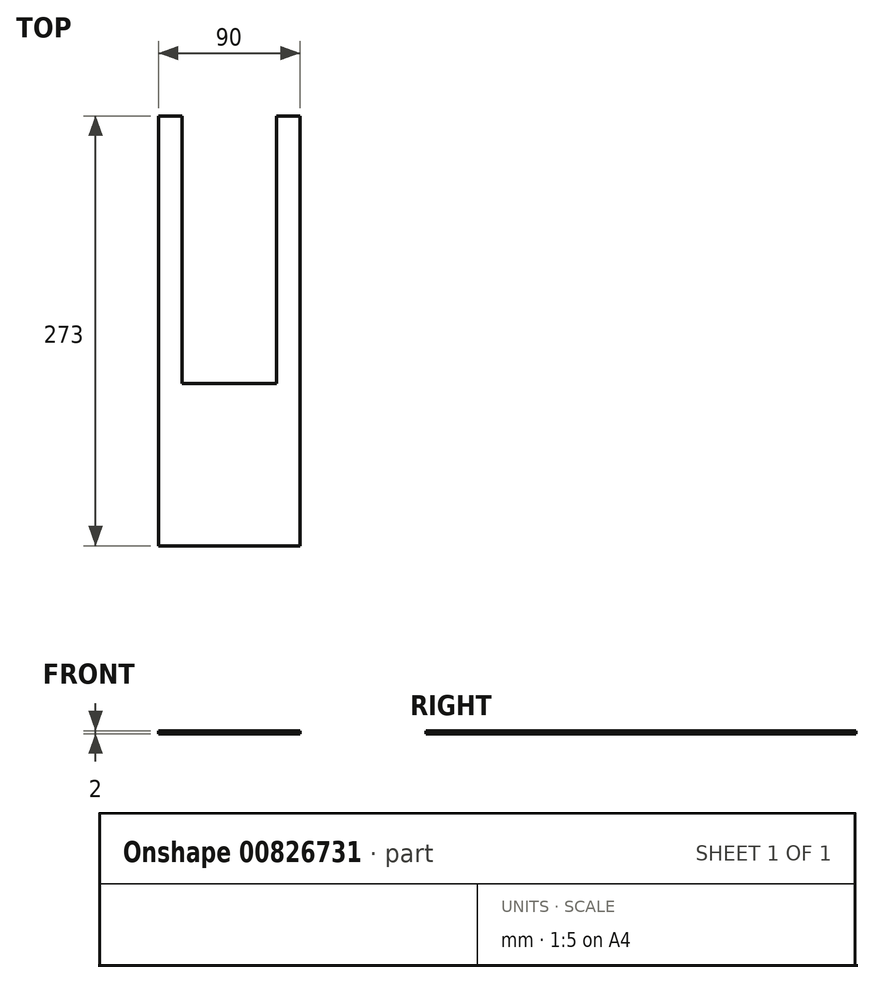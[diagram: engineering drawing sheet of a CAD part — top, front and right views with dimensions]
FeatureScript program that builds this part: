
annotation { "Feature Type Name" : "Feature", "Feature Type Description" : "" }
export const myFeature = defineFeature(function(context is Context, id is Id, definition is map)
    precondition{}
    {
        {
            var Q0;
            Q0=qCreatedBy(makeId("Top.planeOp"),FACE);
            var sketch = newSketch(context, id + "F0", { "sketchPlane" : qUnion([Q0])});
            skLineSegment(sketch, "E0.bottom", {"start": v(45, 136.5) * mm, "end": v(-45, 136.5) * mm});
            skLineSegment(sketch, "E0.top", {"start": v(45, -136.5) * mm, "end": v(-45, -136.5) * mm});
            skLineSegment(sketch, "E0.left", {"start": v(45, 136.5) * mm, "end": v(45, -136.5) * mm});
            skLineSegment(sketch, "E0.right", {"start": v(-45, 136.5) * mm, "end": v(-45, -136.5) * mm});
            skPoint(sketch, "E0.middle", {"position": v(0, 0) * mm});
            skLineSegment(sketch, "E1.bottom", {"start": v(-30, 136.5) * mm, "end": v(30, 136.5) * mm});
            skLineSegment(sketch, "E1.top", {"start": v(-30, -33.5) * mm, "end": v(30, -33.5) * mm});
            skLineSegment(sketch, "E1.left", {"start": v(-30, 136.5) * mm, "end": v(-30, -33.5) * mm});
            skLineSegment(sketch, "E1.right", {"start": v(30, 136.5) * mm, "end": v(30, -33.5) * mm});
            skSolve(sketch);
        }
        {
            var Q0;
            Q0=makeQuery(id+"F0.imprint","IMPRINT",FACE,{"disambiguationData":[TD([[makeQuery(id+"F0.imprint","IMPRINT",EDGE,{"derivedFrom":sQuery(id+"F0.wireOp",EDGE,"E0.top")}),-1.0]])]});
            extrude(context, id + "F1", {"entities" : qUnion([Q0]), "depth" : 2 * mm, "offsetDistance" : 25 * mm});
        }
    });
